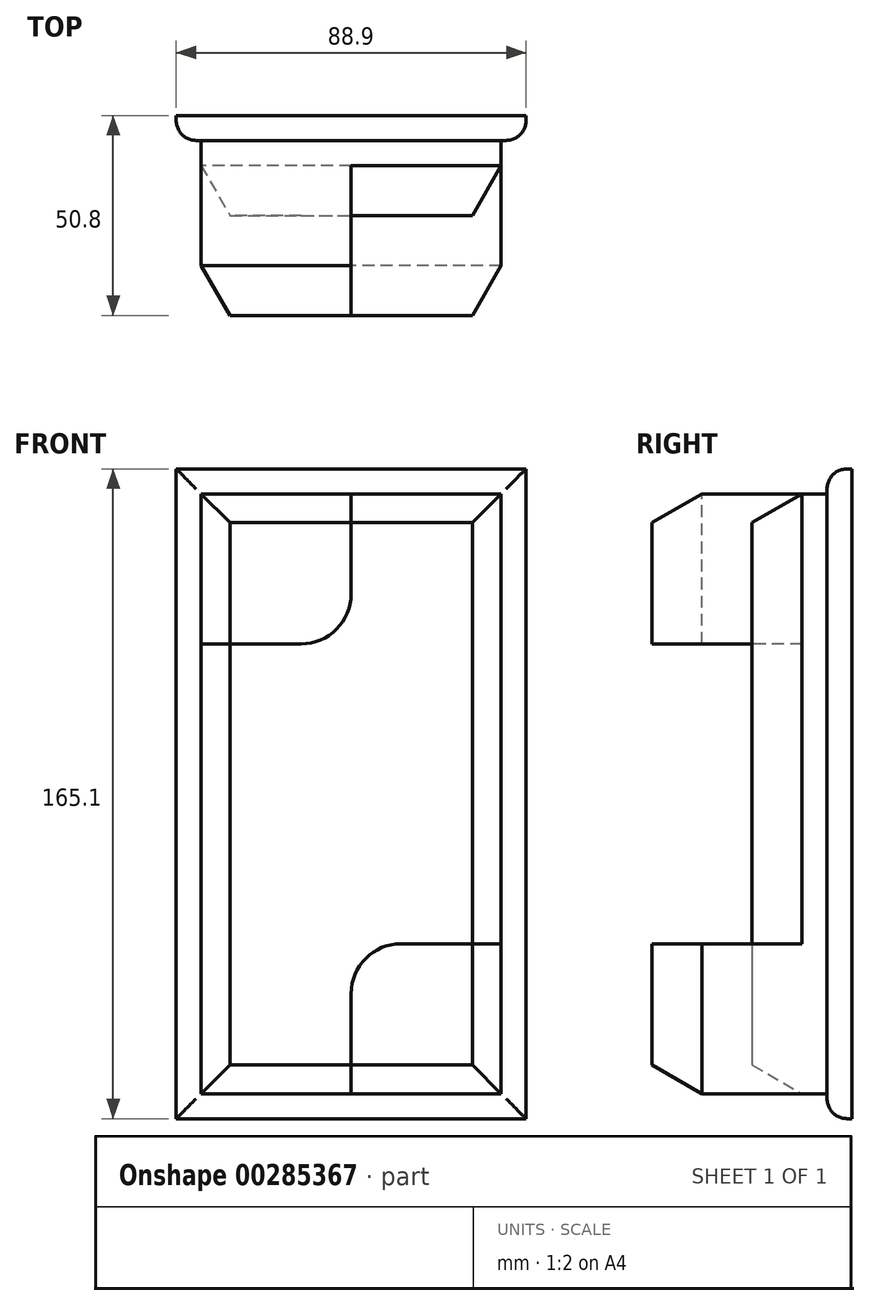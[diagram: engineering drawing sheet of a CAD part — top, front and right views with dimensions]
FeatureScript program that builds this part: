
annotation { "Feature Type Name" : "Feature", "Feature Type Description" : "" }
export const myFeature = defineFeature(function(context is Context, id is Id, definition is map)
    precondition{}
    {
        {
            var Q0;
            Q0=qCreatedBy(makeId("Front.planeOp"),FACE);
            var sketch = newSketch(context, id + "F0", { "sketchPlane" : qUnion([Q0])});
            skLineSegment(sketch, "E0", {"start": v(-47.37, 49.75) * mm, "end": v(-47.37, -102.65) * mm});
            skLineSegment(sketch, "E1", {"start": v(-47.37, -102.65) * mm, "end": v(28.83, -102.65) * mm});
            skLineSegment(sketch, "E2", {"start": v(28.83, -102.65) * mm, "end": v(28.83, 49.75) * mm});
            skLineSegment(sketch, "E3", {"start": v(28.83, 49.75) * mm, "end": v(-47.37, 49.75) * mm});
            skLineSegment(sketch, "E4.0", {"start": v(35.18, 56.1) * mm, "end": v(-53.72, 56.1) * mm});
            skLineSegment(sketch, "E4.1", {"start": v(35.18, -109) * mm, "end": v(35.18, 56.1) * mm});
            skLineSegment(sketch, "E4.2", {"start": v(-53.72, -109) * mm, "end": v(35.18, -109) * mm});
            skLineSegment(sketch, "E4.3", {"start": v(-53.72, 56.1) * mm, "end": v(-53.72, -109) * mm});
            skLineSegment(sketch, "E5", {"start": v(-9.27, 49.75) * mm, "end": v(-9.27, 24.35) * mm});
            skLineSegment(sketch, "E6", {"start": v(-21.97, 11.65) * mm, "end": v(-47.37, 11.65) * mm});
            skLineSegment(sketch, "E7", {"start": v(28.83, -64.55) * mm, "end": v(3.43, -64.55) * mm});
            skLineSegment(sketch, "E8", {"start": v(-9.27, -77.25) * mm, "end": v(-9.27, -102.65) * mm});
            skPoint(sketch, "E9.visualSharp", {"position": v(-9.27, 11.65) * mm});
            skArc(sketch, "E9.filletArc", {"start": v(-21.97, 11.65) * mm, "mid": v(-13, 15.37) * mm, "end": v(-9.27, 24.35) * mm});
            skPoint(sketch, "E10.visualSharp", {"position": v(-9.27, -64.55) * mm});
            skArc(sketch, "E10.filletArc", {"start": v(3.43, -64.55) * mm, "mid": v(-5.55, -68.27) * mm, "end": v(-9.27, -77.25) * mm});
            skSolve(sketch);
        }
        {
            var Q0;
            Q0 = qSketchRegion(id + "F0", true);
            extrude(context, id + "F1", {"entities" : qUnion([Q0]), "depth" : 6.35 * mm});
        }
        {
            var Q0;
            {var subQ9=sQuery(id+"F0.wireOp",EDGE,"E5");Q0=makeQuery(id+"F0.imprint","IMPRINT",FACE,{"disambiguationData":[TD([[makeQuery(id+"F0.imprint","IMPRINT",EDGE,{"derivedFrom":subQ9}),1.0]])]});}
            extrude(context, id + "F2", {"entities" : qUnion([Q0]), "operationType" : NewBodyOperationType.ADD, "depth" : 25.4 * mm});
        }
        {
            var Q0;
            {var subQ1=sQuery(id+"F0.wireOp",EDGE,"E5");Q0=makeQuery(id+"F0.imprint","IMPRINT",FACE,{"disambiguationData":[TD([[makeQuery(id+"F0.imprint","IMPRINT",EDGE,{"derivedFrom":subQ1}),-1.0]])]});}
            var Q1;
            {var subQ4=sQuery(id+"F0.wireOp",EDGE,"E7");Q1=makeQuery(id+"F0.imprint","IMPRINT",FACE,{"disambiguationData":[TD([[makeQuery(id+"F0.imprint","IMPRINT",EDGE,{"derivedFrom":subQ4}),1.0]])]});}
            extrude(context, id + "F3", {"entities" : qUnion([Q0, Q1]), "operationType" : NewBodyOperationType.ADD, "depth" : 50.8 * mm});
        }
        {
            var Q0;
            Q0=makeQuery(id+"F1.opExtrude","CAP_EDGE",EDGE,{"disambiguationData":[OSD([sQuery(id+"F0.wireOp",EDGE,"E4.1")])],"isStart":false});
            var Q1;
            Q1=makeQuery(id+"F1.opExtrude","CAP_EDGE",EDGE,{"disambiguationData":[OSD([sQuery(id+"F0.wireOp",EDGE,"E4.2")])],"isStart":false});
            var Q2;
            Q2=makeQuery(id+"F1.opExtrude","CAP_EDGE",EDGE,{"disambiguationData":[OSD([sQuery(id+"F0.wireOp",EDGE,"E4.3")])],"isStart":false});
            var Q3;
            Q3=makeQuery(id+"F1.opExtrude","CAP_EDGE",EDGE,{"disambiguationData":[OSD([sQuery(id+"F0.wireOp",EDGE,"E4.0")])],"isStart":false});
            fillet(context, id + "F4", {"entities" : qUnion([Q0, Q1, Q2, Q3]), "radius" : 5.08 * mm, "tangentPropagation" : true, "allowEdgeOverflow" : false});
        }
        {
            var Q0;
            Q0=makeQuery(id+"F3.opExtrude","CAP_EDGE",EDGE,{"disambiguationData":[OSD([sQuery(id+"F0.wireOp",EDGE,"E0")])],"isStart":false});
            var Q1;
            Q1=makeQuery(id+"F3.opExtrude","CAP_EDGE",EDGE,{"disambiguationData":[OSD([sQuery(id+"F0.wireOp",EDGE,"E3")])],"isStart":false});
            var Q2;
            Q2=makeQuery(id+"F3.opExtrude","CAP_EDGE",EDGE,{"disambiguationData":[OSD([sQuery(id+"F0.wireOp",EDGE,"E1")])],"isStart":false});
            var Q3;
            Q3=makeQuery(id+"F3.opExtrude","CAP_EDGE",EDGE,{"disambiguationData":[OSD([sQuery(id+"F0.wireOp",EDGE,"E2")])],"isStart":false});
            var Q4;
            Q4=makeQuery(id+"F2.opExtrude","CAP_EDGE",EDGE,{"disambiguationData":[OSD([sQuery(id+"F0.wireOp",EDGE,"E2")])],"isStart":false});
            var Q5;
            Q5=makeQuery(id+"F2.opExtrude","CAP_EDGE",EDGE,{"disambiguationData":[OSD([sQuery(id+"F0.wireOp",EDGE,"E0")])],"isStart":false});
            var Q6;
            Q6=makeQuery(id+"F2.opExtrude","CAP_EDGE",EDGE,{"disambiguationData":[OSD([sQuery(id+"F0.wireOp",EDGE,"E1")])],"isStart":false});
            var Q7;
            Q7=makeQuery(id+"F2.opExtrude","CAP_EDGE",EDGE,{"disambiguationData":[OSD([sQuery(id+"F0.wireOp",EDGE,"E3")])],"isStart":false});
            chamfer(context, id + "F5", {"entities" : qUnion([Q0, Q1, Q2, Q3, Q4, Q5, Q6, Q7]), "chamferType" : ChamferType.OFFSET_ANGLE, "width" : 12.7 * mm, "oppositeDirection" : true, "angle" : 30 * degree, "tangentPropagation" : true});
        }
    });
